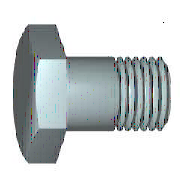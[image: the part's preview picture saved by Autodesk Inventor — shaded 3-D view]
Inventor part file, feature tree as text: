
AUTODESK INVENTOR PART (.ipt)
format: ipt  version: 2020 (Build 240168000, 168)  size: 208,896 bytes
history: native  units: mm (DEFAULTED — no unit token found)
features: sketch x5, extrude x4, plane x2, chamfer x2, thread x1
ambient origin geometry x7: Origin, YZ Plane, XZ Plane, X Axis, Y Axis, Z Axis, Center Point
bodies: Solid1 (feature_tree)
feature tree (14):
  sketch  "草图1"  dims[d2=12.0mm d3=7.5mm]
  plane  "工作平面2"
  extrude  "头"  Depth=12.0mm
  chamfer  "倒角1"  Distance=45.0mm
  plane  "Work Plane1"
  extrude  "拉伸5"  Depth=2.0mm
  extrude  "拉伸6"  TaperAngle=30.0deg  [1 undecoded]
  extrude  "拉伸7"  Depth=2.0mm
  chamfer  "倒角2"  Distance=7.5mm
  thread  "螺纹3"  [1 undecoded]
  sketch  "草图2"  dims[d4=0.0mm]
  sketch  "草图7"  dims[d21=90.0deg]
  sketch  "草图8"  dims[d11=18.0mm]
  sketch  "草图9"  dims[d58=0.0mm d59=45.0mm d65=18.0mm d67=30.0deg d68=21.6mm d69=7.5mm d74=26.0mm d75=3.0mm d76=0.0mm d77=12.0mm d78=2.0mm d79=0.0mm d80=16.0mm d81=12.0mm d82=0.0mm d83=1.5mm d84=2.0mm d85=45.0deg d86=20.0mm d87=0.0mm]
note: 2 required parameter values undecoded (feature->parameter linkage not recoverable at this tier; creation-order binding heuristic only, values carry confidence <= 0.55)
